# Revit family: окна.rehau_эркер_прямоугольный_2-угла
name_source: partatom
category: Окна
revit_build: Autodesk Revit 2017 (Build: 20171027_0315(x64)
units: mm (PartAtom-declared; Revit-internal decimal feet)

## family parameters
Всегда вертикально = Да
Заголовок OmniClass = Windows
Номер OmniClass = 23.30.20.00
Общий = Нет
Основа = Стена
При загрузке вырезать с полостями = Нет
Точка расчета площади = Нет

## types (1)
- Стандарт
    ADSK_Обозначение = ГОСТ 30674-99
    URL = https://www.rehau.com
    Аналитическая конструкция = Окна с одинарным остеклением - для жилых зданий
    Высота подоконника по умолчанию = 600 мм
    Замыкание стены = По основе
    Изготовитель = Rehau
    Изображение типоразмера = <Нет>
    Коэффициент теплопередачи (U) = 5.7361 Вт/(м²·K)
    Коэффициент теплопритока от солнечного излучения = 0.86
    Материал коробки = <По категории>
    Материал отлива = <По категории>
    Материал подоконника = <По категории>
    Описание = эркер.окно
    Примерная высота = 0 мм
    Примерная ширина = 0 мм
    Пропускание видимого света = 0.9
    Термостойкость = 0.1743 (м²·K)/Вт
    профиль_60 = Rehau : 60
    профиль_70 = Rehau : 70
    профиль_70(95) = Rehau : 70 (95)
    профиль_80(117) = Rehau : 80 (117)
